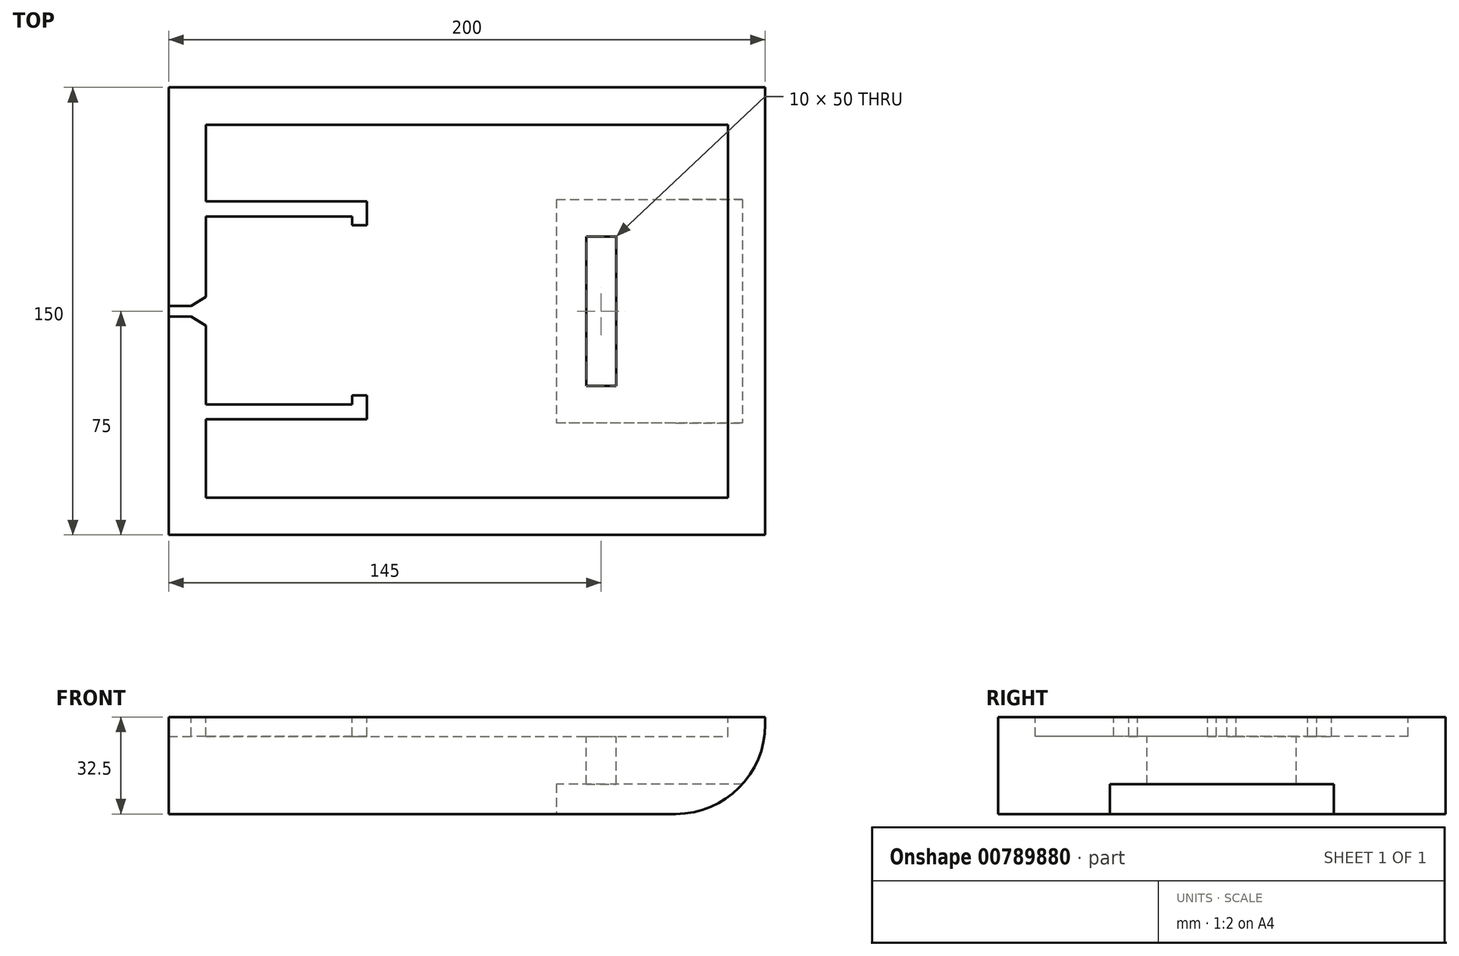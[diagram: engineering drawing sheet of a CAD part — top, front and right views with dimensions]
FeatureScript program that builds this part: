
annotation { "Feature Type Name" : "Feature", "Feature Type Description" : "" }
export const myFeature = defineFeature(function(context is Context, id is Id, definition is map)
    precondition{}
    {
        {
            var Q0;
            Q0=qCreatedBy(makeId("Front.planeOp"),FACE);
            var sketch = newSketch(context, id + "F0", { "sketchPlane" : qUnion([Q0])});
            skLineSegment(sketch, "E0.bottom", {"start": v(100, 16.25) * mm, "end": v(-100, 16.25) * mm});
            skLineSegment(sketch, "E0.top", {"start": v(70, -16.25) * mm, "end": v(-100, -16.25) * mm});
            skLineSegment(sketch, "E0.left", {"start": v(100, 16.25) * mm, "end": v(100, 13.75) * mm});
            skLineSegment(sketch, "E0.right", {"start": v(-100, 16.25) * mm, "end": v(-100, -16.25) * mm});
            skPoint(sketch, "E0.middle", {"position": v(0, 0) * mm});
            skPoint(sketch, "E1.visualSharp", {"position": v(100, -16.25) * mm});
            skArc(sketch, "E1.filletArc", {"start": v(70, -16.25) * mm, "mid": v(91.21, -7.46) * mm, "end": v(100, 13.75) * mm});
            skSolve(sketch);
        }
        {
            var Q0;
            Q0=qSketchRegion(id+"F0",true);
            extrude(context, id + "F1", {"entities" : qUnion([Q0]), "endBound" : BoundingType.SYMMETRIC, "oppositeDirection" : true, "depth" : 150 * mm});
        }
        {
            var Q0;
            Q0=makeQuery(id+"F1.opExtrude","SWEPT_FACE",FACE,{"disambiguationData":[OSD([sQuery(id+"F0.wireOp",EDGE,"E0.bottom")])]});
            var sketch = newSketch(context, id + "F2", { "sketchPlane" : qUnion([Q0])});
            skLineSegment(sketch, "E2.bottom", {"start": v(87.5, 62.5) * mm, "end": v(-87.5, 62.5) * mm});
            skLineSegment(sketch, "E2.top", {"start": v(87.5, -62.5) * mm, "end": v(-77.5, -62.5) * mm});
            skLineSegment(sketch, "E2.left", {"start": v(87.5, 62.5) * mm, "end": v(87.5, -62.5) * mm});
            skLineSegment(sketch, "E2.right", {"start": v(-87.5, 62.5) * mm, "end": v(-87.5, 36.79) * mm});
            skPoint(sketch, "E2.middle", {"position": v(0, 0) * mm});
            skLineSegment(sketch, "E3.bottom", {"start": v(-87.5, 31.79) * mm, "end": v(-46, 31.79) * mm});
            skLineSegment(sketch, "E4", {"start": v(-46, -36.21) * mm, "end": v(-87.5, -36.21) * mm});
            skLineSegment(sketch, "E5", {"start": v(-41, -36.21) * mm, "end": v(-46, -36.21) * mm});
            skLineSegment(sketch, "E6", {"start": v(-41, 36.79) * mm, "end": v(-87.5, 36.79) * mm});
            skLineSegment(sketch, "E7.trimOffspring", {"start": v(-87.5, -36.21) * mm, "end": v(-87.5, -62.5) * mm});
            skLineSegment(sketch, "E8", {"start": v(-6, -28.21) * mm, "end": v(-6, 28.79) * mm});
            skLineSegment(sketch, "E9", {"start": v(-87.5, -62.5) * mm, "end": v(-77.5, -62.5) * mm});
            skLineSegment(sketch, "E10", {"start": v(-87.5, 31.79) * mm, "end": v(-38.5, 31.79) * mm});
            skLineSegment(sketch, "E11", {"start": v(-38.5, 31.79) * mm, "end": v(-38.5, 28.79) * mm});
            skLineSegment(sketch, "E12", {"start": v(-38.5, 28.79) * mm, "end": v(-33.5, 28.79) * mm});
            skLineSegment(sketch, "E13", {"start": v(-33.5, 28.79) * mm, "end": v(-33.5, 36.79) * mm});
            skLineSegment(sketch, "E14", {"start": v(-33.5, 36.79) * mm, "end": v(-41, 36.79) * mm});
            skLineSegment(sketch, "E15", {"start": v(-100, 1.8) * mm, "end": v(-100, -1.8) * mm});
            skLineSegment(sketch, "E16", {"start": v(-100, 1.8) * mm, "end": v(-92.5, 1.8) * mm});
            skLineSegment(sketch, "E17", {"start": v(-100, -1.8) * mm, "end": v(-92.5, -1.8) * mm});
            skLineSegment(sketch, "E18", {"start": v(-87.5, -4.8) * mm, "end": v(-92.5, -1.8) * mm});
            skLineSegment(sketch, "E19", {"start": v(-92.5, 1.8) * mm, "end": v(-87.5, 4.8) * mm});
            skLineSegment(sketch, "E20", {"start": v(-87.5, 4.8) * mm, "end": v(-87.5, 31.79) * mm});
            skLineSegment(sketch, "E21", {"start": v(-87.5, -4.8) * mm, "end": v(-87.5, -31.21) * mm});
            skLineSegment(sketch, "E22", {"start": v(-87.5, -31.21) * mm, "end": v(-38.5, -31.21) * mm});
            skLineSegment(sketch, "E23", {"start": v(-38.5, -31.21) * mm, "end": v(-38.5, -28.21) * mm});
            skLineSegment(sketch, "E24", {"start": v(-38.5, -28.21) * mm, "end": v(-33.5, -28.21) * mm});
            skLineSegment(sketch, "E25", {"start": v(-33.5, -28.21) * mm, "end": v(-33.5, -36.21) * mm});
            skLineSegment(sketch, "E26", {"start": v(-33.5, -36.21) * mm, "end": v(-41, -36.21) * mm});
            skPoint(sketch, "E27.start.orphan", {"position": v(-41, -28.21) * mm});
            skLineSegment(sketch, "E28", {"start": v(0, 0) * mm, "end": v(40, 0) * mm});
            skLineSegment(sketch, "E29", {"start": v(40, 0) * mm, "end": v(40, 37.5) * mm});
            skLineSegment(sketch, "E30", {"start": v(40, 0) * mm, "end": v(40, -37.5) * mm});
            skPoint(sketch, "E31.end.orphan", {"position": v(42.98, -37.5) * mm});
            skLineSegment(sketch, "E32", {"start": v(40, 37.5) * mm, "end": v(50, 37.5) * mm});
            skLineSegment(sketch, "E33", {"start": v(50, 37.5) * mm, "end": v(50, -37.5) * mm});
            skLineSegment(sketch, "E34", {"start": v(50, -37.5) * mm, "end": v(40, -37.5) * mm});
            skLineSegment(sketch, "E35", {"start": v(40, 0) * mm, "end": v(40, 25) * mm});
            skLineSegment(sketch, "E36", {"start": v(40, 25) * mm, "end": v(50, 25) * mm});
            skLineSegment(sketch, "E37", {"start": v(40, 0) * mm, "end": v(40, -25) * mm});
            skLineSegment(sketch, "E38", {"start": v(40, -25) * mm, "end": v(50, -25) * mm});
            skSolve(sketch);
        }
        {
            var Q0;
            Q0=makeQuery(id+"F2.imprint","IMPRINT",FACE,{"disambiguationData":[TD([[makeQuery(id+"F2.imprint","IMPRINT",EDGE,{"derivedFrom":sQuery(id+"F2.wireOp",EDGE,"E2.bottom")}),1.0]])]});
            var Q1;
            Q1=makeQuery(id+"F2.imprint","IMPRINT",FACE,{"disambiguationData":[TD([[makeQuery(id+"F2.imprint","IMPRINT",EDGE,{"derivedFrom":sQuery(id+"F2.wireOp",EDGE,"E29")}),-1.0]])]});
            var Q2;
            Q2=makeQuery(id+"F2.imprint","IMPRINT",FACE,{"disambiguationData":[TD([[makeQuery(id+"F2.imprint","IMPRINT",EDGE,{"derivedFrom":sQuery(id+"F2.wireOp",EDGE,"E30")}),1.0]])]});
            extrude(context, id + "F3", {"entities" : qUnion([Q0, Q1, Q2]), "operationType" : NewBodyOperationType.REMOVE, "oppositeDirection" : true, "depth" : 6.5 * mm, "offsetDistance" : 25 * mm});
        }
        {
            var Q0;
            Q0=makeQuery(id+"F3.boolean.opBoolean","SPLIT",FACE,{"disambiguationData":[TD([makeQuery(id+"F3.opExtrude","SWEPT_FACE",FACE,{"disambiguationData":[OSD([sQuery(id+"F2.wireOp",EDGE,"E33")])]})])],"derivedFrom":makeQuery(id+"F1.opExtrude","SWEPT_FACE",FACE,{"disambiguationData":[OSD([sQuery(id+"F0.wireOp",EDGE,"E0.bottom")])]})});
            extrude(context, id + "F4", {"entities" : qUnion([Q0]), "operationType" : NewBodyOperationType.REMOVE, "oppositeDirection" : true, "depth" : 9000 * mm, "offsetDistance" : 25 * mm});
        }
        {
            var Q0;
            Q0=makeQuery(id+"F1.opExtrude","SWEPT_FACE",FACE,{"disambiguationData":[OSD([sQuery(id+"F0.wireOp",EDGE,"E0.top")])]});
            var sketch = newSketch(context, id + "F5", { "sketchPlane" : qUnion([Q0])});
            skLineSegment(sketch, "E39", {"start": v(0, 0) * mm, "end": v(30, 0) * mm});
            skLineSegment(sketch, "E40", {"start": v(30, 0) * mm, "end": v(30, 37.5) * mm});
            skLineSegment(sketch, "E41", {"start": v(30, 0) * mm, "end": v(30, -37.5) * mm});
            skLineSegment(sketch, "E42", {"start": v(30, -37.5) * mm, "end": v(100, -37.5) * mm});
            skLineSegment(sketch, "E43", {"start": v(100, -37.5) * mm, "end": v(100, 37.5) * mm});
            skLineSegment(sketch, "E44", {"start": v(100, 37.5) * mm, "end": v(30, 37.5) * mm});
            skSolve(sketch);
        }
        {
            var Q0;
            {var subQ0=sQuery(id+"F5.wireOp",EDGE,"E43");Q0=makeQuery(id+"F5.imprint","IMPRINT",FACE,{"disambiguationData":[TD([[makeQuery(id+"F5.imprint","IMPRINT",EDGE,{"derivedFrom":subQ0}),1.0]])]});}
            var Q1;
            {var subQ7=sQuery(id+"F5.wireOp",EDGE,"E40");Q1=makeQuery(id+"F5.imprint","IMPRINT",FACE,{"disambiguationData":[TD([[makeQuery(id+"F5.imprint","IMPRINT",EDGE,{"derivedFrom":subQ7}),-1.0]])]});}
            extrude(context, id + "F6", {"entities" : qUnion([Q0, Q1]), "operationType" : NewBodyOperationType.REMOVE, "oppositeDirection" : true, "depth" : 10 * mm, "offsetDistance" : 25 * mm});
        }
    });
